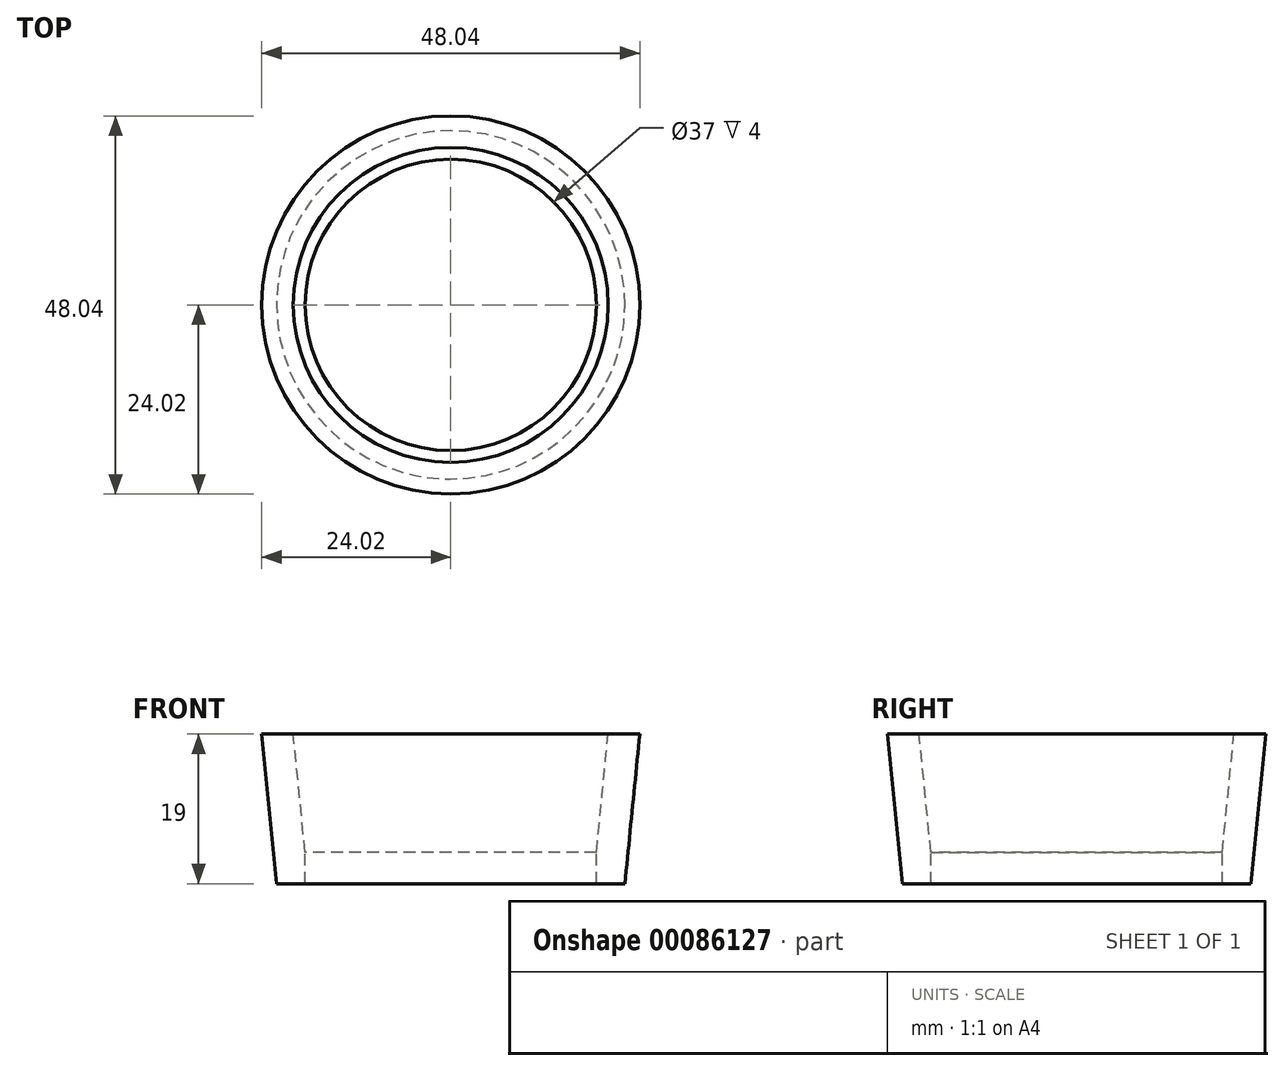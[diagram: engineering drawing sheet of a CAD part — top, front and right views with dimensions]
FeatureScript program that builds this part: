
annotation { "Feature Type Name" : "Feature", "Feature Type Description" : "" }
export const myFeature = defineFeature(function(context is Context, id is Id, definition is map)
    precondition{}
    {
        {
            var Q0;
            Q0=qCreatedBy(makeId("Top.planeOp"),FACE);
            var sketch = newSketch(context, id + "F0", { "sketchPlane" : qUnion([Q0])});
            skCircle(sketch, "E0", {"center": v(0, 0) * mm, "radius": 18.5 * mm});
            skSolve(sketch);
        }
        {
            var Q0;
            Q0=qCreatedBy(makeId("Top.planeOp"),FACE);
            cPlane(context, id + "F1", {"entities" : qUnion([Q0]), "cplaneType" : CPlaneType.OFFSET, "offset" : 15 * mm, "width" : 150 * mm, "height" : 150 * mm});
        }
        {
            var Q0;
            Q0=qCreatedBy(id+"F1.planeOp",FACE);
            var sketch = newSketch(context, id + "F2", { "sketchPlane" : qUnion([Q0])});
            skCircle(sketch, "E1", {"center": v(0, 0) * mm, "radius": 20 * mm});
            skSolve(sketch);
        }
        {
            var Q0;
            Q0=makeQuery(id+"F0.imprint","IMPRINT",FACE,{"disambiguationData":[TD([[makeQuery(id+"F0.imprint","IMPRINT",EDGE,{"derivedFrom":sQuery(id+"F0.wireOp",EDGE,"E0")}),1.0]])]});
            var Q1;
            Q1=makeQuery(id+"F2.imprint","IMPRINT",FACE,{"disambiguationData":[TD([[makeQuery(id+"F2.imprint","IMPRINT",EDGE,{"derivedFrom":sQuery(id+"F2.wireOp",EDGE,"E1")}),1.0]])]});
            loft(context, id + "F3", {"sheetProfilesArray" : [{ "sheetProfileEntities" : qUnion([Q0]) }, { "sheetProfileEntities" : qUnion([Q1]) }]});
        }
        {
            var Q0;
            Q0=makeQuery(id+"F3.opLoft","CAP_FACE",FACE,{"disambiguationData":[OSD([makeQuery(id+"F2.imprint","IMPRINT",FACE,{"disambiguationData":[TD([[makeQuery(id+"F2.imprint","IMPRINT",EDGE,{"derivedFrom":sQuery(id+"F2.wireOp",EDGE,"E1")}),1.0]])]})])],"isStart":true});
            shell(context, id + "F4", {"entities" : qUnion([Q0]), "thickness" : 4 * mm, "oppositeDirection" : true});
        }
        {
            var Q0;
            Q0=makeQuery(id+"F4.opShell","OFFSET_FACE",FACE,{"disambiguationData":[OSD([makeQuery(id+"F0.imprint","IMPRINT",FACE,{"disambiguationData":[TD([[makeQuery(id+"F0.imprint","IMPRINT",EDGE,{"derivedFrom":sQuery(id+"F0.wireOp",EDGE,"E0")}),1.0]])]})])]});
            var sketch = newSketch(context, id + "F5", { "sketchPlane" : qUnion([Q0])});
            skCircle(sketch, "E2", {"center": v(0, 0) * mm, "radius": 18.5 * mm});
            skSolve(sketch);
        }
        {
            var Q0;
            Q0 = qSketchRegion(id + "F5", true);
            extrude(context, id + "F6", {"entities" : qUnion([Q0]), "operationType" : NewBodyOperationType.REMOVE, "oppositeDirection" : true, "depth" : 25 * mm});
        }
    });
